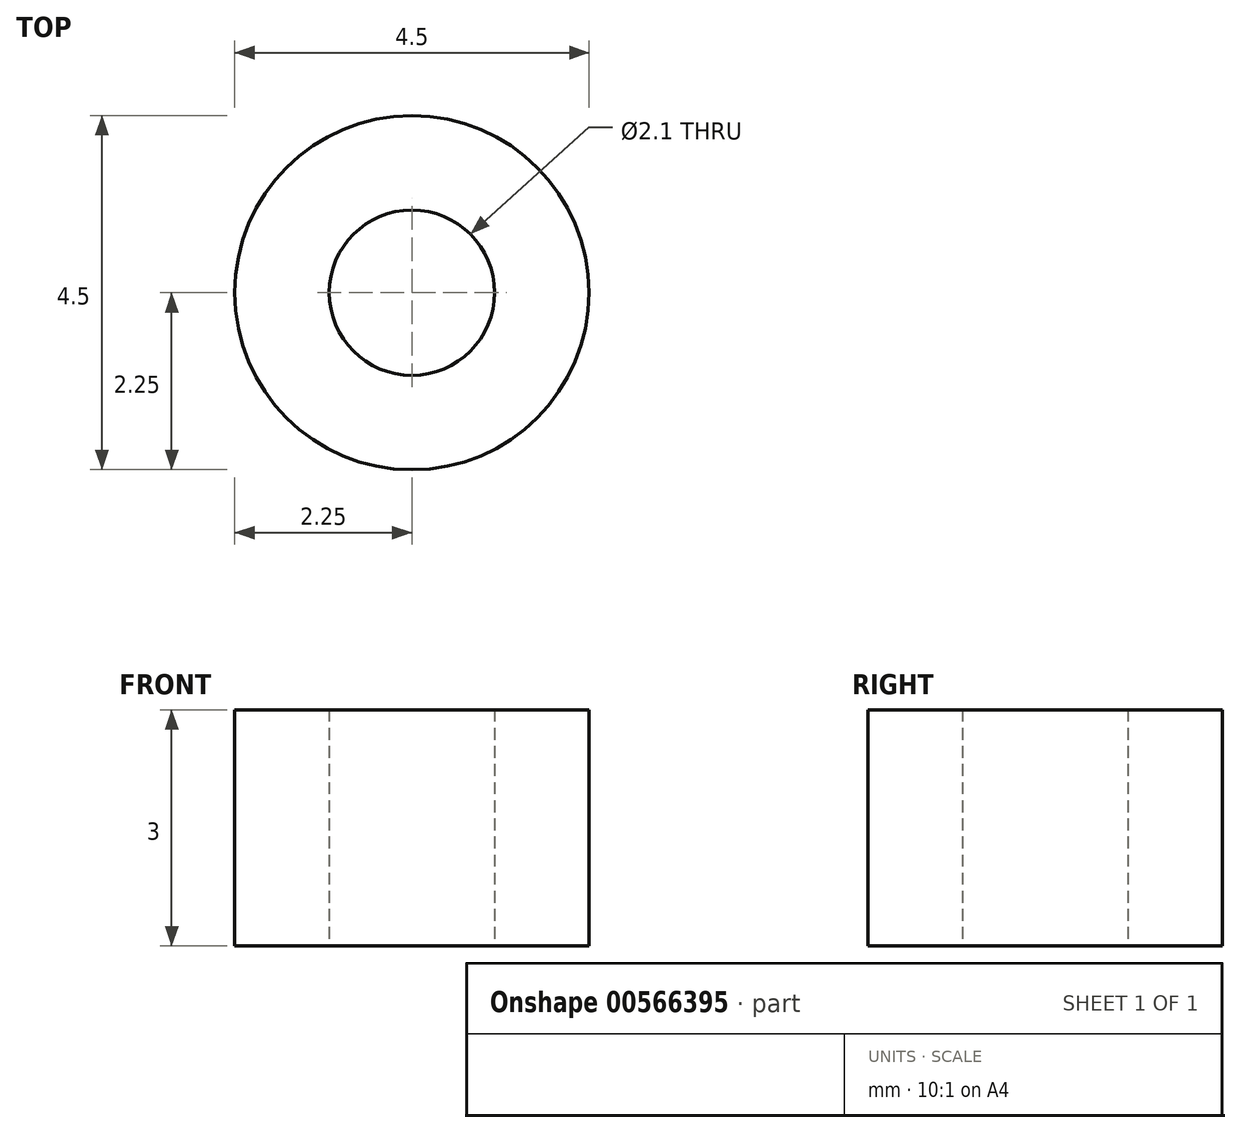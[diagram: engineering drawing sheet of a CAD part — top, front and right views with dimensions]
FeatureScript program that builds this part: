
annotation { "Feature Type Name" : "Feature", "Feature Type Description" : "" }
export const myFeature = defineFeature(function(context is Context, id is Id, definition is map)
    precondition{}
    {
        {
            var Q0;
            Q0=qCreatedBy(makeId("Top.planeOp"),FACE);
            var sketch = newSketch(context, id + "F0", { "sketchPlane" : qUnion([Q0])});
            skCircle(sketch, "E0", {"center": v(0, 0) * mm, "radius": 1.05 * mm});
            skCircle(sketch, "E1", {"center": v(0, 0) * mm, "radius": 2.25 * mm});
            skSolve(sketch);
        }
        {
            var Q0;
            Q0 = qSketchRegion(id + "F0", true);
            extrude(context, id + "F1", {"entities" : qUnion([Q0]), "depth" : 3 * mm, "offsetDistance" : 25 * mm});
        }
    });
